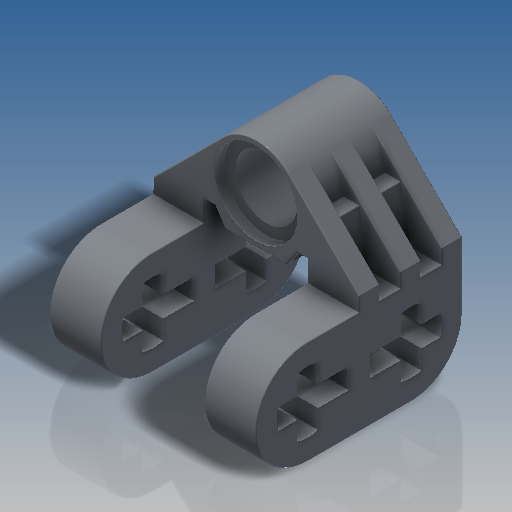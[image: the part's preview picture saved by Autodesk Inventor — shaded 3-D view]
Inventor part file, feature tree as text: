
AUTODESK INVENTOR PART (.ipt)
format: ipt  version: 2019.4 (Build 234330000, 330)  size: 516,608 bytes
history: native  units: in
note: dims shown in document units (in); Inventor stores cm internally (conversion verified against a paired STEP export)
features: extrude x5, sketch x3, pattern_linear x1, mirror x1, fillet x1
ambient origin geometry x8: Origin, YZ Plane, XZ Plane, XY Plane, X Axis, Y Axis, Z Axis, Center Point
bodies: Solid1 (feature_tree)
feature tree (11):
  sketch  "Sketch1"  dims[d0=0.189in d1=0.252in]
  extrude  "Extrusion1"  Depth=0.189in
  extrude  "Extrusion2"  Depth=0.6299in
  pattern_linear  "Rectangular Pattern1"  Spacing1=90.0deg  [1 undecoded]
  extrude  "Extrusion3"  Depth=0.1575in
  extrude  "Extrusion4"  Depth=0.189in
  extrude  "Extrusion5"  TaperAngle=0.0deg  [1 undecoded]
  mirror  "Mirror1"
  fillet  "Fillet1"  Radius=0.063in
  sketch  "Sketch2"  dims[d2=0.2835in d3=0.6299in]
  sketch  "Sketch3"  dims[d4=0.1575in d6=90.0deg d7=0.1575in d8=0.315in d9=0.0in d10=0.063in d11=0.0in d12=1.1811in d14=0.252in d15=0.0315in d16=0.0in d17=0.252in d18=0.0315in d19=0.0in d20=0.315in d21=0.189in d22=0.063in d23=0.1575in d24=0.0in d25=0.063in d26=0.0039in d27=0.378in d28=0.4409in d29=0.063in d30=0.189in d31=0.252in]
note: 2 required parameter values undecoded (feature->parameter linkage not recoverable at this tier; creation-order binding heuristic only, values carry confidence <= 0.55)
